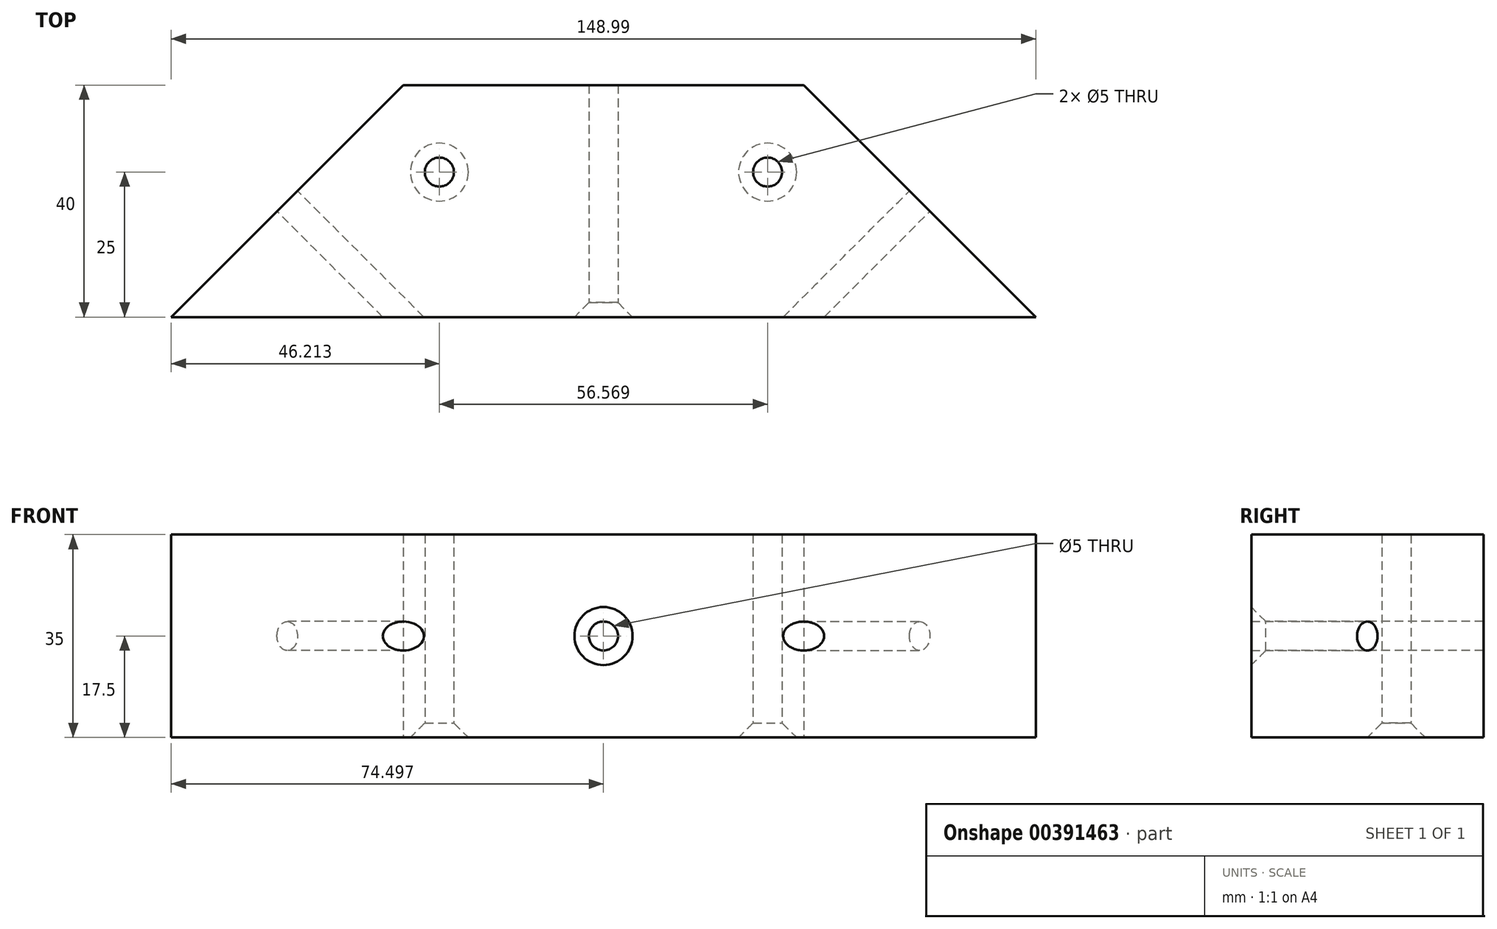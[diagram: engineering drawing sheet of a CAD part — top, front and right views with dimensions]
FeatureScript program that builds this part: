
annotation { "Feature Type Name" : "Feature", "Feature Type Description" : "" }
export const myFeature = defineFeature(function(context is Context, id is Id, definition is map)
    precondition{}
    {
        {
            var Q0;
            Q0=qCreatedBy(makeId("Top.planeOp"),FACE);
            var sketch = newSketch(context, id + "F0", { "sketchPlane" : qUnion([Q0])});
            skLineSegment(sketch, "E0.bottom", {"start": v(0, 0) * mm, "end": v(149, 0) * mm});
            skLineSegment(sketch, "E0.top", {"start": v(40, 40) * mm, "end": v(109, 40) * mm});
            skLineSegment(sketch, "E1", {"start": v(149, 0) * mm, "end": v(109, 40) * mm});
            skLineSegment(sketch, "E2", {"start": v(0, 0) * mm, "end": v(40, 40) * mm});
            skSolve(sketch);
        }
        {
            var Q0;
            Q0=makeQuery(id+"F0.imprint","IMPRINT",FACE,{"disambiguationData":[TD([[makeQuery(id+"F0.imprint","IMPRINT",EDGE,{"derivedFrom":sQuery(id+"F0.wireOp",EDGE,"E0.bottom")}),1.0]])]});
            extrude(context, id + "F1", {"entities" : qUnion([Q0]), "depth" : 35 * mm});
        }
        {
            var Q0;
            Q0=makeQuery(id+"F1.opExtrude","SWEPT_FACE",FACE,{"disambiguationData":[OSD([sQuery(id+"F0.wireOp",EDGE,"E0.bottom")])]});
            var sketch = newSketch(context, id + "F2", { "sketchPlane" : qUnion([Q0])});
            skPoint(sketch, "E3", {"position": v(74.5, 17.5) * mm});
            skSolve(sketch);
        }
        {
            var Q0;
            Q0=sQuery(id+"F2.wireOp",VERTEX,"E3");
            var Q1;
            Q1=makeQuery(id+"F1.opExtrude","SWEPT_BODY",BODY,{"disambiguationData":[OSD([sQuery(id+"F0.wireOp",EDGE,"E0.bottom"),sQuery(id+"F0.wireOp",EDGE,"E0.top"),sQuery(id+"F0.wireOp",EDGE,"E1"),sQuery(id+"F0.wireOp",EDGE,"E2")])]});
            hole(context, id + "F3", {"style" : HoleStyle.C_SINK, "endStyle" : HoleEndStyle.THROUGH, "holeDiameter" : 5 * mm, "cSinkDiameter" : 10 * mm, "cSinkAngle" : 90 * degree, "isTappedThrough" : true, "tappedDepth" : 12 * mm, "tapClearance" : 3, "startFromSketch" : true, "locations" : qUnion([Q0]), "scope" : qUnion([Q1])});
        }
        {
            var Q0;
            Q0=makeQuery(id+"F1.opExtrude","SWEPT_FACE",FACE,{"disambiguationData":[OSD([sQuery(id+"F0.wireOp",EDGE,"E1")])]});
            var sketch = newSketch(context, id + "F4", { "sketchPlane" : qUnion([Q0])});
            skPoint(sketch, "E4", {"position": v(-77.07, 17.5) * mm});
            skLineSegment(sketch, "E5", {"start": v(-77.07, 17.5) * mm, "end": v(-105.36, 17.5) * mm, "construction": true});
            skLineSegment(sketch, "E6", {"start": v(-77.07, 17.5) * mm, "end": v(-48.79, 17.5) * mm, "construction": true});
            skSolve(sketch);
        }
        {
            var Q0;
            Q0=makeQuery(id+"F1.opExtrude","SWEPT_FACE",FACE,{"disambiguationData":[OSD([sQuery(id+"F0.wireOp",EDGE,"E2")])]});
            var sketch = newSketch(context, id + "F5", { "sketchPlane" : qUnion([Q0])});
            skLineSegment(sketch, "E7", {"start": v(-56.57, 17.5) * mm, "end": v(-28.28, 17.5) * mm, "construction": true});
            skLineSegment(sketch, "E8", {"start": v(-28.28, 17.5) * mm, "end": v(-28.28, 0) * mm, "construction": true});
            skPoint(sketch, "E9.orphan", {"position": v(0, 17.5) * mm});
            skLineSegment(sketch, "E10", {"start": v(-28.28, 17.5) * mm, "end": v(0, 17.5) * mm, "construction": true});
            skLineSegment(sketch, "E11", {"start": v(-28.28, 17.5) * mm, "end": v(-28.28, 35) * mm, "construction": true});
            skPoint(sketch, "E12", {"position": v(-28.28, 17.5) * mm});
            skSolve(sketch);
        }
        {
            var Q0;
            Q0=sQuery(id+"F5.wireOp",VERTEX,"E12");
            var Q1;
            Q1=makeQuery(id+"F1.opExtrude","SWEPT_BODY",BODY,{"disambiguationData":[OSD([sQuery(id+"F0.wireOp",EDGE,"E0.bottom"),sQuery(id+"F0.wireOp",EDGE,"E0.top"),sQuery(id+"F0.wireOp",EDGE,"E1"),sQuery(id+"F0.wireOp",EDGE,"E2")])]});
            hole(context, id + "F6", {"style" : HoleStyle.SIMPLE, "endStyle" : HoleEndStyle.THROUGH, "holeDiameter" : 5 * mm, "isTappedThrough" : true, "tappedDepth" : 12 * mm, "tapClearance" : 3, "startFromSketch" : true, "locations" : qUnion([Q0]), "scope" : qUnion([Q1])});
        }
        {
            var Q0;
            Q0=sQuery(id+"F4.wireOp",VERTEX,"E4");
            var Q1;
            Q1=makeQuery(id+"F1.opExtrude","SWEPT_BODY",BODY,{"disambiguationData":[OSD([sQuery(id+"F0.wireOp",EDGE,"E0.bottom"),sQuery(id+"F0.wireOp",EDGE,"E0.top"),sQuery(id+"F0.wireOp",EDGE,"E1"),sQuery(id+"F0.wireOp",EDGE,"E2")])]});
            hole(context, id + "F7", {"style" : HoleStyle.SIMPLE, "endStyle" : HoleEndStyle.THROUGH, "holeDiameter" : 5 * mm, "isTappedThrough" : true, "tappedDepth" : 12 * mm, "tapClearance" : 3, "startFromSketch" : true, "locations" : qUnion([Q0]), "scope" : qUnion([Q1])});
        }
        {
            var Q0;
            Q0=makeQuery(id+"F1.opExtrude","CAP_FACE",FACE,{"disambiguationData":[OSD([sQuery(id+"F0.wireOp",EDGE,"E0.bottom"),sQuery(id+"F0.wireOp",EDGE,"E0.top"),sQuery(id+"F0.wireOp",EDGE,"E1"),sQuery(id+"F0.wireOp",EDGE,"E2")])],"isStart":true});
            var sketch = newSketch(context, id + "F8", { "sketchPlane" : qUnion([Q0])});
            skLineSegment(sketch, "E13", {"start": v(129, -25) * mm, "end": v(4.87, -25) * mm, "construction": true});
            skPoint(sketch, "E13.startSnap0", {"position": v(129, -20) * mm});
            skLineSegment(sketch, "E14", {"start": v(113.39, -35.6) * mm, "end": v(102.78, -25) * mm, "construction": true});
            skLineSegment(sketch, "E15", {"start": v(35.6, -35.6) * mm, "end": v(46.21, -25) * mm, "construction": true});
            skPoint(sketch, "E16", {"position": v(102.78, -25) * mm});
            skPoint(sketch, "E17", {"position": v(46.21, -25) * mm});
            skSolve(sketch);
        }
        {
            var Q0;
            Q0=sQuery(id+"F8.wireOp",VERTEX,"E16");
            var Q1;
            Q1=sQuery(id+"F8.wireOp",VERTEX,"E17");
            var Q2;
            Q2=makeQuery(id+"F1.opExtrude","SWEPT_BODY",BODY,{"disambiguationData":[OSD([sQuery(id+"F0.wireOp",EDGE,"E0.bottom"),sQuery(id+"F0.wireOp",EDGE,"E0.top"),sQuery(id+"F0.wireOp",EDGE,"E1"),sQuery(id+"F0.wireOp",EDGE,"E2")])]});
            hole(context, id + "F9", {"style" : HoleStyle.C_SINK, "endStyle" : HoleEndStyle.THROUGH, "holeDiameter" : 5 * mm, "cSinkDiameter" : 10 * mm, "cSinkAngle" : 90 * degree, "isTappedThrough" : true, "tappedDepth" : 12 * mm, "tapClearance" : 3, "startFromSketch" : true, "locations" : qUnion([Q0, Q1]), "scope" : qUnion([Q2])});
        }
    });
